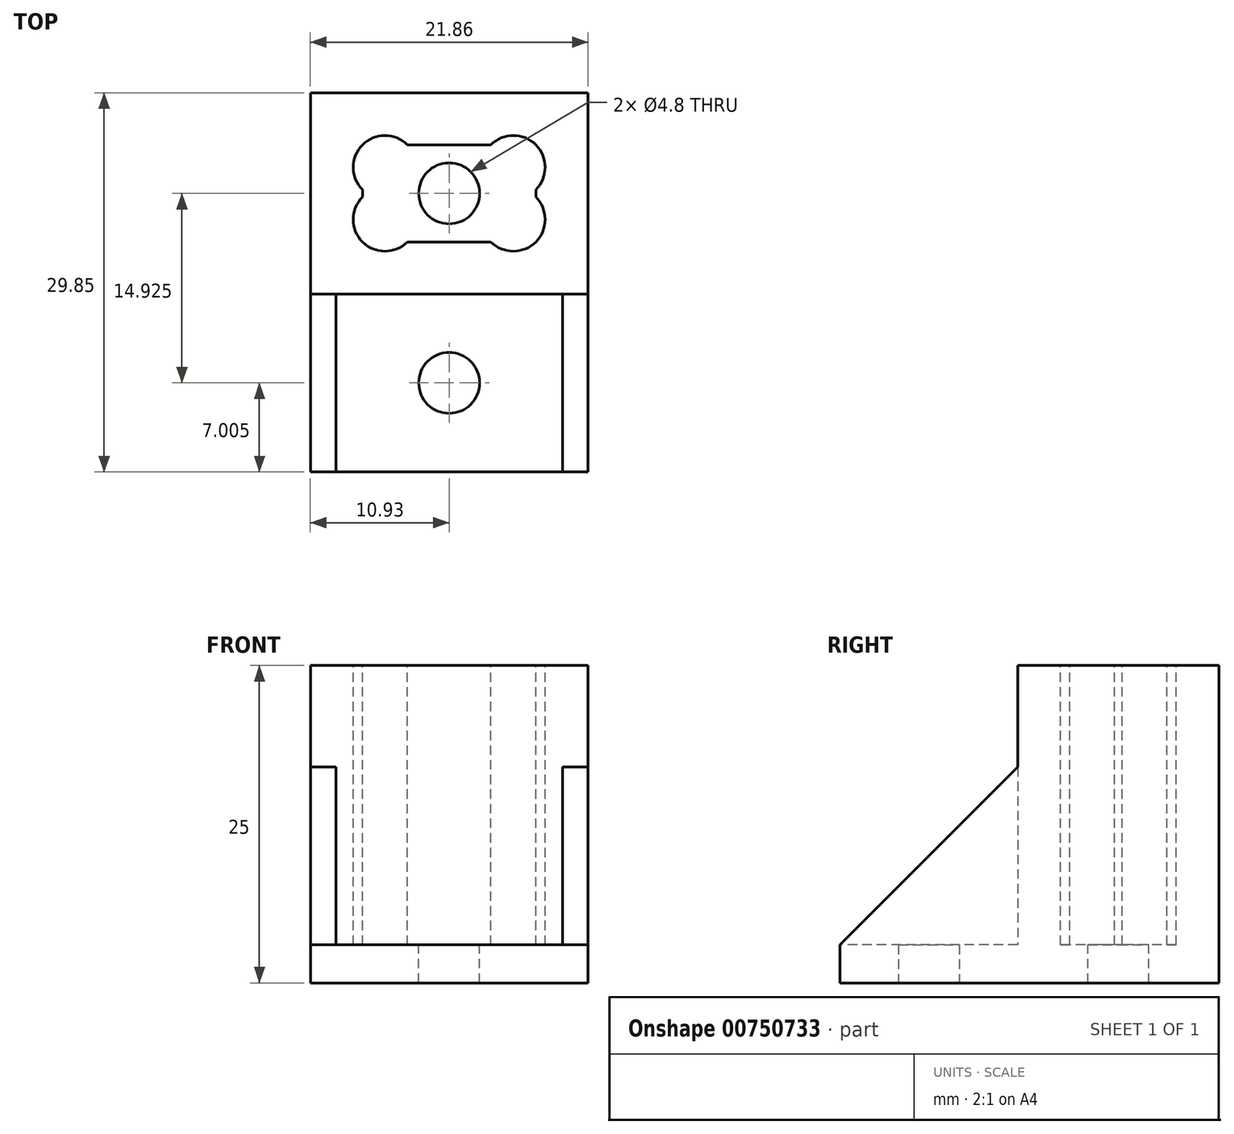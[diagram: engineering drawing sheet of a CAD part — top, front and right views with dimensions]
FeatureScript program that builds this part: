
annotation { "Feature Type Name" : "Feature", "Feature Type Description" : "" }
export const myFeature = defineFeature(function(context is Context, id is Id, definition is map)
    precondition{}
    {
        {
            var Q0;
            Q0=qCreatedBy(makeId("Top.planeOp"),FACE);
            var sketch = newSketch(context, id + "F0", { "sketchPlane" : qUnion([Q0])});
            skLineSegment(sketch, "E0.bottom", {"start": v(6.82, -3.83) * mm, "end": v(-6.83, -3.83) * mm, "construction": true});
            skLineSegment(sketch, "E0.top", {"start": v(6.83, 3.83) * mm, "end": v(-6.82, 3.82) * mm, "construction": true});
            skLineSegment(sketch, "E0.left", {"start": v(6.82, -3.83) * mm, "end": v(6.83, 3.83) * mm, "construction": true});
            skLineSegment(sketch, "E0.right", {"start": v(-6.83, -3.83) * mm, "end": v(-6.82, 3.82) * mm, "construction": true});
            skPoint(sketch, "E0.middle", {"position": v(0, 0) * mm});
            skLineSegment(sketch, "E1.0", {"start": v(10.92, -7.92) * mm, "end": v(-10.93, -7.93) * mm});
            skLineSegment(sketch, "E1.1", {"start": v(10.92, -7.92) * mm, "end": v(10.93, 7.93) * mm});
            skLineSegment(sketch, "E1.2", {"start": v(10.93, 7.93) * mm, "end": v(-10.93, 7.92) * mm});
            skLineSegment(sketch, "E1.3", {"start": v(-10.93, -7.93) * mm, "end": v(-10.93, 7.92) * mm});
            skSolve(sketch);
        }
        {
            var Q0;
            Q0=qSketchRegion(id+"F0",true);
            extrude(context, id + "F1", {"entities" : qUnion([Q0]), "depth" : 25 * mm, "offsetDistance" : 25 * mm});
        }
        {
            var Q0;
            Q0=makeQuery(id+"F1.opExtrude","CAP_FACE",FACE,{"disambiguationData":[OSD([sQuery(id+"F0.wireOp",EDGE,"E1.0"),sQuery(id+"F0.wireOp",EDGE,"E1.1"),sQuery(id+"F0.wireOp",EDGE,"E1.2"),sQuery(id+"F0.wireOp",EDGE,"E1.3")])],"isStart":false});
            var sketch = newSketch(context, id + "F2", { "sketchPlane" : qUnion([Q0])});
            skLineSegment(sketch, "E2.0", {"start": v(-6.83, -3.83) * mm, "end": v(-6.83, -0.29) * mm, "construction": true});
            skLineSegment(sketch, "E2.1", {"start": v(6.82, -3.83) * mm, "end": v(6.82, -0.29) * mm, "construction": true});
            skLineSegment(sketch, "E2.2", {"start": v(6.82, -3.83) * mm, "end": v(3.29, -3.83) * mm, "construction": true});
            skLineSegment(sketch, "E2.3", {"start": v(6.83, 3.83) * mm, "end": v(3.29, 3.83) * mm, "construction": true});
            skArc(sketch, "E3", {"start": v(-3.29, 3.83) * mm, "mid": v(-6.82, 3.82) * mm, "end": v(-6.82, 0.29) * mm});
            skArc(sketch, "E4", {"start": v(6.82, 0.29) * mm, "mid": v(6.83, 3.83) * mm, "end": v(3.29, 3.83) * mm});
            skLineSegment(sketch, "E5", {"start": v(3.29, -3.83) * mm, "end": v(3.29, -3.83) * mm});
            skArc(sketch, "E6", {"start": v(-6.82, -0.29) * mm, "mid": v(-6.83, -3.83) * mm, "end": v(-3.29, -3.83) * mm});
            skLineSegment(sketch, "E7", {"start": v(-6.82, 0.29) * mm, "end": v(-6.82, 3.82) * mm, "construction": true});
            skLineSegment(sketch, "E8", {"start": v(-3.29, 3.83) * mm, "end": v(-6.82, 3.82) * mm, "construction": true});
            skLineSegment(sketch, "E9", {"start": v(3.29, 3.83) * mm, "end": v(-3.29, 3.83) * mm});
            skLineSegment(sketch, "E10", {"start": v(6.83, 0.29) * mm, "end": v(6.83, 3.83) * mm, "construction": true});
            skLineSegment(sketch, "E11", {"start": v(6.83, -0.29) * mm, "end": v(6.83, 0.29) * mm});
            skLineSegment(sketch, "E12", {"start": v(-3.29, -3.83) * mm, "end": v(-6.83, -3.83) * mm, "construction": true});
            skLineSegment(sketch, "E13", {"start": v(-6.82, -0.29) * mm, "end": v(-6.82, 0.29) * mm});
            skArc(sketch, "E14", {"start": v(3.29, -3.83) * mm, "mid": v(6.82, -3.83) * mm, "end": v(6.82, -0.29) * mm});
            skLineSegment(sketch, "E15", {"start": v(3.29, -3.83) * mm, "end": v(-3.29, -3.83) * mm});
            skLineSegment(sketch, "E16", {"start": v(-5.06, 2.06) * mm, "end": v(-6.82, 3.82) * mm, "construction": true});
            skSolve(sketch);
        }
        {
            var Q0;
            Q0=qSketchRegion(id+"F2",true);
            var Q1;
            Q1=makeQuery(id+"F1.opExtrude","CAP_FACE",FACE,{"disambiguationData":[OSD([sQuery(id+"F0.wireOp",EDGE,"E1.0"),sQuery(id+"F0.wireOp",EDGE,"E1.1"),sQuery(id+"F0.wireOp",EDGE,"E1.2"),sQuery(id+"F0.wireOp",EDGE,"E1.3")])],"isStart":true});
            extrude(context, id + "F3", {"entities" : qUnion([Q0]), "operationType" : NewBodyOperationType.REMOVE, "endBound" : BoundingType.UP_TO_SURFACE, "oppositeDirection" : true, "depth" : 25 * mm, "endBoundEntityFace" : qUnion([Q1]), "hasOffset" : true, "offsetDistance" : 3 * mm});
        }
        {
            var Q0;
            Q0=makeQuery(id+"F3.boolean.opBoolean","COPY",FACE,{"derivedFrom":makeQuery(id+"F3.opExtrude","CAP_FACE",FACE,{"disambiguationData":[OSD([sQuery(id+"F2.wireOp",EDGE,"E3"),sQuery(id+"F2.wireOp",EDGE,"E4"),sQuery(id+"F2.wireOp",EDGE,"E6"),sQuery(id+"F2.wireOp",EDGE,"E9"),sQuery(id+"F2.wireOp",EDGE,"E11"),sQuery(id+"F2.wireOp",EDGE,"E13"),sQuery(id+"F2.wireOp",EDGE,"E14"),sQuery(id+"F2.wireOp",EDGE,"E15")])],"isStart":false})});
            var sketch = newSketch(context, id + "F4", { "sketchPlane" : qUnion([Q0])});
            skCircle(sketch, "E17", {"center": v(0, 0) * mm, "radius": 2.4 * mm});
            skSolve(sketch);
        }
        {
            var Q0;
            Q0=qSketchRegion(id+"F4",true);
            extrude(context, id + "F5", {"entities" : qUnion([Q0]), "operationType" : NewBodyOperationType.REMOVE, "endBound" : BoundingType.THROUGH_ALL, "oppositeDirection" : true, "depth" : 25 * mm, "offsetDistance" : 25 * mm});
        }
        {
            var Q0;
            Q0=qCreatedBy(makeId("Top.planeOp"),FACE);
            var sketch = newSketch(context, id + "F6", { "sketchPlane" : qUnion([Q0])});
            skLineSegment(sketch, "E18.0", {"start": v(10.92, -7.92) * mm, "end": v(-10.93, -7.93) * mm});
            skLineSegment(sketch, "E19.bottom", {"start": v(-10.93, -7.93) * mm, "end": v(10.92, -7.92) * mm});
            skLineSegment(sketch, "E19.top", {"start": v(-10.93, -21.93) * mm, "end": v(10.92, -21.93) * mm});
            skLineSegment(sketch, "E19.left", {"start": v(-10.93, -7.93) * mm, "end": v(-10.93, -21.92) * mm});
            skLineSegment(sketch, "E19.right", {"start": v(10.93, -7.92) * mm, "end": v(10.93, -21.93) * mm});
            skLineSegment(sketch, "E20", {"start": v(0, -7.92) * mm, "end": v(0, -21.93) * mm, "construction": true});
            skCircle(sketch, "E21", {"center": v(0, -14.92) * mm, "radius": 2.4 * mm});
            skCircle(sketch, "E22", {"center": v(0, -14.92) * mm, "radius": 7 * mm, "construction": true});
            skSolve(sketch);
        }
        {
            var Q0;
            Q0 = qSketchRegion(id + "F6", true);
            extrude(context, id + "F7", {"entities" : qUnion([Q0]), "operationType" : NewBodyOperationType.ADD, "depth" : 3 * mm, "offsetDistance" : 25 * mm});
        }
        {
            var Q0;
            Q0=makeQuery(id+"F7.boolean.opBoolean","MERGE",FACE,{"derivedFrom":[makeQuery(id+"F1.opExtrude","SWEPT_FACE",FACE,{"disambiguationData":[OSD([sQuery(id+"F0.wireOp",EDGE,"E1.3")])]}),makeQuery(id+"F7.opExtrude","SWEPT_FACE",FACE,{"disambiguationData":[OSD([sQuery(id+"F6.wireOp",EDGE,"E19.left")])]})]});
            var sketch = newSketch(context, id + "F8", { "sketchPlane" : qUnion([Q0])});
            skLineSegment(sketch, "E23.0", {"start": v(7.93, 25) * mm, "end": v(7.93, 3) * mm});
            skLineSegment(sketch, "E23.1", {"start": v(7.93, 3) * mm, "end": v(21.93, 3) * mm});
            skLineSegment(sketch, "E24", {"start": v(21.93, 3) * mm, "end": v(7.92, 17) * mm});
            skSolve(sketch);
        }
        {
            var Q0;
            Q0 = qSketchRegion(id + "F8", true);
            extrude(context, id + "F9", {"entities" : qUnion([Q0]), "operationType" : NewBodyOperationType.ADD, "oppositeDirection" : true, "depth" : 2 * mm, "offsetDistance" : 25 * mm});
        }
        {
            var Q0;
            Q0=makeQuery(id+"F7.boolean.opBoolean","MERGE",FACE,{"derivedFrom":[makeQuery(id+"F1.opExtrude","SWEPT_FACE",FACE,{"disambiguationData":[OSD([sQuery(id+"F0.wireOp",EDGE,"E1.1")])]}),makeQuery(id+"F7.opExtrude","SWEPT_FACE",FACE,{"disambiguationData":[OSD([sQuery(id+"F6.wireOp",EDGE,"E19.right")])]})]});
            var sketch = newSketch(context, id + "F10", { "sketchPlane" : qUnion([Q0])});
            skLineSegment(sketch, "E25.0", {"start": v(-7.92, 25) * mm, "end": v(-7.92, 3) * mm});
            skLineSegment(sketch, "E25.1", {"start": v(-7.92, 3) * mm, "end": v(-21.93, 3) * mm});
            skLineSegment(sketch, "E26.0", {"start": v(-21.93, 3) * mm, "end": v(-7.92, 17) * mm});
            skSolve(sketch);
        }
        {
            var Q0;
            Q0 = qSketchRegion(id + "F10", true);
            extrude(context, id + "F11", {"entities" : qUnion([Q0]), "operationType" : NewBodyOperationType.ADD, "oppositeDirection" : true, "depth" : 2 * mm, "offsetDistance" : 25 * mm});
        }
    });
